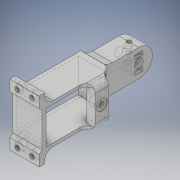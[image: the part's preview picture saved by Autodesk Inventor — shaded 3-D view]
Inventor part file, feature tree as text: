
AUTODESK INVENTOR PART (.ipt)
format: ipt  version: 2019 (Build 230136000, 136)  size: 389,632 bytes
history: native  units: mm
features: sketch x14, extrude x10, hole x4, fillet x4, chamfer x2, plane x2, mirror x2
ambient origin geometry x8: Origin, YZ Plane, XZ Plane, XY Plane, X Axis, Y Axis, Z Axis, Center Point
bodies: Solid1 (feature_tree)
feature tree (38):
  extrude  "Extrusion1"  Depth=29.9mm
  extrude  "Extrusion2"  Depth=10.0mm
  extrude  "Extrusion4"  Depth=5.795264mm
  extrude  "Extrusion5"  Depth=10.0mm
  chamfer  "Chamfer1"  Distance=13.5mm
  extrude  "Extrusion6"  Depth=1.5mm TaperAngle=0.0deg
  extrude  "Extrusion8"  Depth=10.0mm
  hole  "Hole3"  [1 undecoded]
  hole  "Hole4"  [1 undecoded]
  fillet  "Fillet1"  Radius=8.0mm
  fillet  "Fillet2"  Radius=2.95mm
  fillet  "Fillet3"  Radius=6.3mm
  plane  "Work Plane1"
  extrude  "Extrusion9"  Depth=10.1mm
  hole  "Hole5"  [1 undecoded]
  mirror  "Mirror1"
  fillet  "Fillet5"  Radius=10.1mm
  chamfer  "Chamfer2"  Distance=5.0mm
  extrude  "Extrusion10"  Depth=2.8mm
  extrude  "Extrusion12"  [1 undecoded]
  hole  "Hole6"  [1 undecoded]
  plane  "Work Plane3"
  extrude  "Extrusion13"  Depth=2.8mm
  mirror  "Mirror2"
  sketch  "Sketch1"  dims[d0=20.0mm d1=29.9mm]
  sketch  "Sketch3"  dims[d2=3.1mm d3=10.0mm]
  sketch  "Sketch5"  dims[d4=2.95mm d5=5.795264mm]
  sketch  "Sketch6"  dims[d6=10.0mm d7=12.0mm d8=13.5mm d9=0.0mm]
  sketch  "Sketch8"  dims[d19=1.5mm d20=1.5mm d21=0.0mm]
  sketch  "Sketch11"  dims[d26=24.6mm d27=10.0mm]
  sketch  "Sketch12"  dims[d28=45.0mm d29=50.0mm]
  sketch  "Sketch13"  dims[d30=29.1mm d31=10.0mm d32=0.0mm d33=8.0mm d34=0.0mm]
  sketch  "Sketch14"  dims[d35=6.0mm d36=2.0mm d37=45.0deg d38=2.95mm d39=6.3mm]
  sketch  "Sketch15"  dims[d40=6.0mm d41=0.0mm d53=10.1mm]
  sketch  "Sketch16"  dims[d54=10.0mm d55=6.0mm d56=0.0mm d57=10.1mm]
  sketch  "Sketch18"  dims[d58=4.0mm d59=6.0mm d60=8.0mm d61=0.35mm d62=90.0deg d63=10.0mm d64=0.0mm]
  sketch  "Sketch19"  dims[d65=7.0mm d66=6.0mm d67=8.0mm d68=1.0mm d69=90.0deg d70=4.0mm d71=0.0mm]
  sketch  "Sketch20"  dims[d72=5.0mm d73=5.0mm d74=10.5mm d75=-2.0mm d76=8.0mm d77=8.0mm d78=4.0mm d79=0.0mm d81=3.5mm d82=6.0mm d83=6.0mm d84=2.0mm d85=90.0deg d86=8.0mm d87=20.594885mm d88=6.0mm d89=2.0mm d90=2.0mm d91=45.0deg d92=1.0mm d93=0.0mm d99=10.0mm d100=0.0mm d101=3.1mm d102=6.0mm d103=4.0mm d104=2.0mm d105=90.0deg d106=10.0mm d107=0.0mm d108=-5.0mm d109=5.9mm d110=2.8mm d111=0.0mm]
note: 5 required parameter values undecoded (feature->parameter linkage not recoverable at this tier; creation-order binding heuristic only, values carry confidence <= 0.55)
